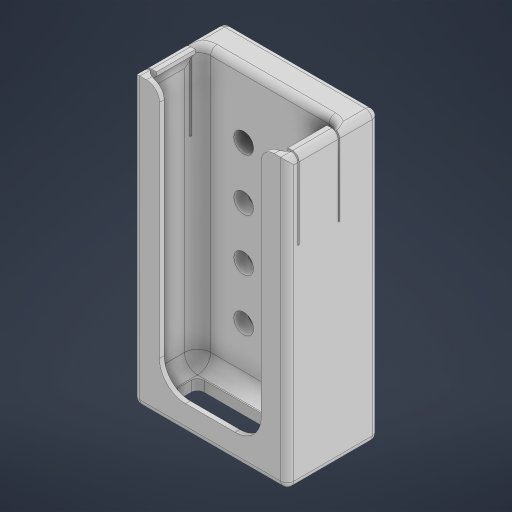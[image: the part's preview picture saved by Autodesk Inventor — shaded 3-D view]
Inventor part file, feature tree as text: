
AUTODESK INVENTOR PART (.ipt)
format: ipt  version: 2023 (Build 270158000, 158)  size: 391,680 bytes
history: native  units: in
note: dims shown in document units (in); Inventor stores cm internally (conversion verified against a paired STEP export)
features: sketch x7, extrude x6, fillet x4, projected_geometry x2, mirror x1, hole x1, pattern_linear x1
ambient origin geometry x8: Origin, YZ Plane, XZ Plane, XY Plane, X Axis, Y Axis, Z Axis, Center Point
bodies: Solid1 (feature_tree)
feature tree (22):
  extrude  "Extrusion1"  Depth=5.3in
  extrude  "Extrusion2"  Depth=1.75in TaperAngle=0.0deg
  extrude  "Extrusion3"  Depth=0.09in
  fillet  "Fillet1"  Radius=0.09in
  extrude  "Extrusion4"  Depth=5.3in TaperAngle=0.0deg
  extrude  "Extrusion5"  Depth=0.5in
  mirror  "Mirror1"
  extrude  "Extrusion6"  Depth=0.5in TaperAngle=0.0deg
  hole  "Hole1"  [1 undecoded]
  pattern_linear  "Rectangular Pattern1"  Spacing1=0.025in  [1 undecoded]
  fillet  "Fillet2"  Radius=0.025in
  fillet  "Fillet3"  Radius=0.75in
  fillet  "Fillet4"  Radius=1.5in
  sketch  "Sketch1"  dims[d0=2.75in d1=5.3in]
  sketch  "Sketch2"  dims[d2=0.1in d3=1.75in d4=0.0in]
  sketch  "Sketch3"  dims[d5=0.09in d6=0.09in d7=0.09in]
  sketch  "Sketch4"  dims[d8=1.05in d9=5.3in d10=0.0in]
  sketch  "Sketch5"  dims[d11=0.5in d12=0.5in]
  projected_geometry  "Projected Loop1"
  sketch  "Sketch6"  dims[d13=0.5in d14=5.25in d15=0.0in]
  projected_geometry  "Projected Loop2"
  sketch  "Sketch7"  dims[d16=0.25in d17=0.2in d18=0.025in d19=0.025in d20=0.75in d21=1.5in d22=0.0in d23=0.0in d30=1.0in d31=0.0in d32=0.125in d33=0.05in d35=0.375in d36=0.375in d37=0.025in d38=0.025in d39=1.0in d40=0.0in d42=0.5in d43=1.5in d44=0.156in d45=0.38in d46=0.375in d47=0.25in d48=0.5635in d49=1.0in d50=0.8108in d51=0.7874in d53=1.0in d54=1.5748in d56=1.0in d57=0.5in d58=0.25in d59=0.125in]
note: 2 required parameter values undecoded (feature->parameter linkage not recoverable at this tier; creation-order binding heuristic only, values carry confidence <= 0.55)
